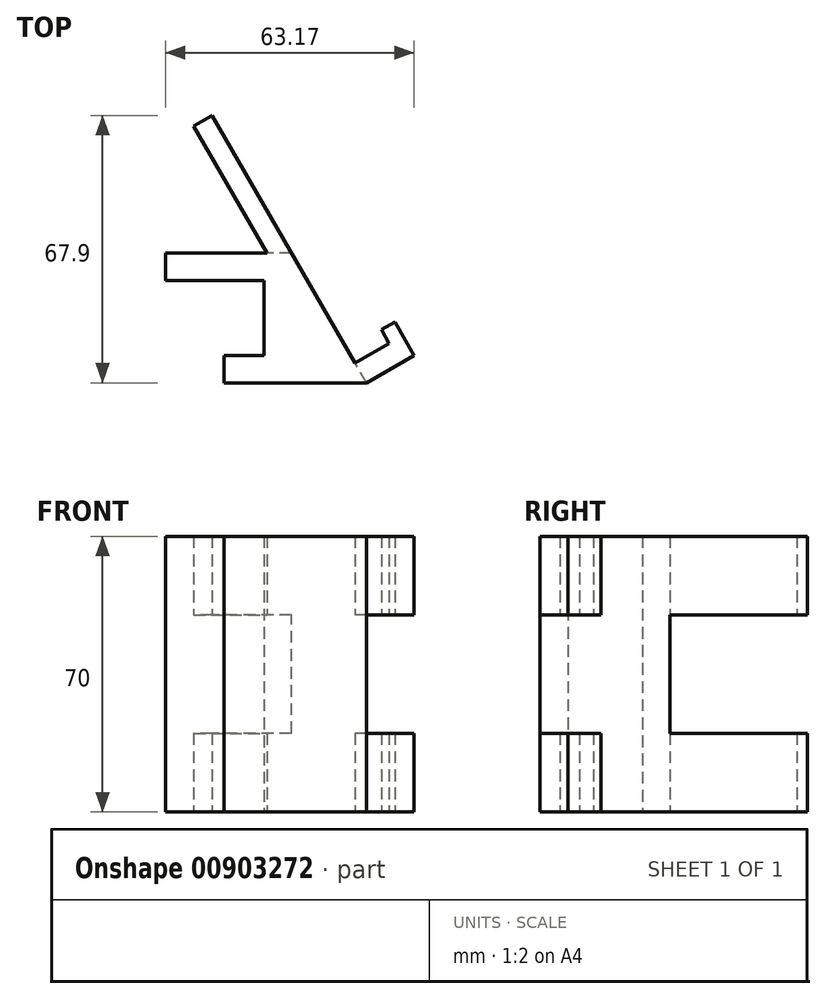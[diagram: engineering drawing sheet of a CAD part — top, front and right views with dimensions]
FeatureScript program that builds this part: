
annotation { "Feature Type Name" : "Feature", "Feature Type Description" : "" }
export const myFeature = defineFeature(function(context is Context, id is Id, definition is map)
    precondition{}
    {
        {
            var Q0;
            Q0=qCreatedBy(makeId("Top.planeOp"),FACE);
            var sketch = newSketch(context, id + "F0", { "sketchPlane" : qUnion([Q0])});
            skLineSegment(sketch, "E0", {"start": v(-43.57, 23.37) * mm, "end": v(-3.06, 23.37) * mm});
            skLineSegment(sketch, "E1", {"start": v(-3.06, 23.37) * mm, "end": v(-3.06, 4.37) * mm});
            skLineSegment(sketch, "E2", {"start": v(-3.06, 4.37) * mm, "end": v(-14.06, 4.37) * mm});
            skLineSegment(sketch, "E3", {"start": v(-14.06, 4.37) * mm, "end": v(-14.06, -10.56) * mm});
            skLineSegment(sketch, "E4", {"start": v(-14.06, -10.56) * mm, "end": v(-29.7, -10.56) * mm});
            skLineSegment(sketch, "E5", {"start": v(-29.7, -10.56) * mm, "end": v(-29.7, 4.37) * mm});
            skLineSegment(sketch, "E6", {"start": v(-29.7, 4.37) * mm, "end": v(-43.57, 4.37) * mm});
            skLineSegment(sketch, "E7", {"start": v(-43.57, 4.37) * mm, "end": v(-43.57, 20.72) * mm});
            skLineSegment(sketch, "E8", {"start": v(-13.06, 4.37) * mm, "end": v(-2.91, 4.37) * mm});
            skLineSegment(sketch, "E9", {"start": v(-2.91, 4.37) * mm, "end": v(-2.91, 23.37) * mm});
            skLineSegment(sketch, "E10", {"start": v(-2.91, 23.37) * mm, "end": v(-27.91, 23.37) * mm});
            skLineSegment(sketch, "E11", {"start": v(-13.06, 4.37) * mm, "end": v(-13.06, -2.63) * mm});
            skLineSegment(sketch, "E12", {"start": v(-13.06, -2.63) * mm, "end": v(4.09, -2.63) * mm});
            skLineSegment(sketch, "E13", {"start": v(4.09, -2.63) * mm, "end": v(4.09, 30.37) * mm});
            skLineSegment(sketch, "E14", {"start": v(4.09, 30.37) * mm, "end": v(-27.91, 30.37) * mm});
            skLineSegment(sketch, "E15", {"start": v(-27.91, 30.37) * mm, "end": v(-27.91, 23.37) * mm});
            skLineSegment(sketch, "E16", {"start": v(23.14, -2.63) * mm, "end": v(4.09, 30.37) * mm});
            skLineSegment(sketch, "E17", {"start": v(4.09, -2.63) * mm, "end": v(23.14, -2.63) * mm});
            skLineSegment(sketch, "E18", {"start": v(23.14, -2.63) * mm, "end": v(31.8, 2.37) * mm});
            skLineSegment(sketch, "E19", {"start": v(31.8, 2.37) * mm, "end": v(28.91, 7.37) * mm});
            skLineSegment(sketch, "E20", {"start": v(28.91, 7.37) * mm, "end": v(20.25, 2.37) * mm});
            skLineSegment(sketch, "E21", {"start": v(4.09, 30.37) * mm, "end": v(-16.06, 65.27) * mm});
            skLineSegment(sketch, "E22", {"start": v(-16.06, 65.27) * mm, "end": v(-20.77, 62.56) * mm});
            skLineSegment(sketch, "E23", {"start": v(-20.77, 62.56) * mm, "end": v(-1.9, 29.86) * mm});
            skLineSegment(sketch, "E24", {"start": v(31.8, 2.37) * mm, "end": v(35.26, 4.37) * mm});
            skLineSegment(sketch, "E25", {"start": v(35.26, 4.37) * mm, "end": v(30.38, 12.83) * mm});
            skLineSegment(sketch, "E26", {"start": v(30.38, 12.83) * mm, "end": v(26.96, 10.86) * mm});
            skLineSegment(sketch, "E27", {"start": v(26.96, 10.86) * mm, "end": v(28.91, 7.37) * mm});
            skSolve(sketch);
        }
        {
            var Q0;
            {var subQ0=sQuery(id+"F0.wireOp",EDGE,"E21");Q0=makeQuery(id+"F0.imprint","IMPRINT",FACE,{"disambiguationData":[TD([[makeQuery(id+"F0.imprint","IMPRINT",EDGE,{"derivedFrom":subQ0}),1.0]])]});}
            var Q1;
            Q1=makeQuery(id+"F0.imprint","IMPRINT",FACE,{"disambiguationData":[TD([[makeQuery(id+"F0.imprint","IMPRINT",EDGE,{"derivedFrom":sQuery(id+"F0.wireOp",EDGE,"E8")}),-1.0]])]});
            var Q2;
            {var subQ0=sQuery(id+"F0.wireOp",EDGE,"E13");Q2=makeQuery(id+"F0.imprint","IMPRINT",FACE,{"disambiguationData":[TD([[makeQuery(id+"F0.imprint","IMPRINT",EDGE,{"derivedFrom":subQ0}),-1.0]])]});}
            var Q3;
            {var subQ0=sQuery(id+"F0.wireOp",EDGE,"E18");Q3=makeQuery(id+"F0.imprint","IMPRINT",FACE,{"disambiguationData":[TD([[makeQuery(id+"F0.imprint","IMPRINT",EDGE,{"derivedFrom":subQ0}),1.0]])]});}
            var Q4;
            Q4=makeQuery(id+"F0.imprint","IMPRINT",FACE,{"disambiguationData":[TD([[makeQuery(id+"F0.imprint","IMPRINT",EDGE,{"derivedFrom":sQuery(id+"F0.wireOp",EDGE,"E19")}),-1.0]])]});
            extrude(context, id + "F1", {"entities" : qUnion([Q0, Q1, Q2, Q3, Q4]), "depth" : 20 * mm, "offsetDistance" : 25 * mm});
        }
        {
            var Q0;
            {var subQ0=sQuery(id+"F0.wireOp",EDGE,"E21");Q0=makeQuery(id+"F0.imprint","IMPRINT",FACE,{"disambiguationData":[TD([[makeQuery(id+"F0.imprint","IMPRINT",EDGE,{"derivedFrom":subQ0}),1.0]])]});}
            var Q1;
            {var subQ10=sQuery(id+"F0.wireOp",EDGE,"E9");Q1=makeQuery(id+"F0.imprint","IMPRINT",FACE,{"disambiguationData":[TD([[makeQuery(id+"F0.imprint","IMPRINT",EDGE,{"derivedFrom":subQ10}),-1.0]])]});}
            var Q2;
            {var subQ0=sQuery(id+"F0.wireOp",EDGE,"E13");Q2=makeQuery(id+"F0.imprint","IMPRINT",FACE,{"disambiguationData":[TD([[makeQuery(id+"F0.imprint","IMPRINT",EDGE,{"derivedFrom":subQ0}),-1.0]])]});}
            var Q3;
            {var subQ0=sQuery(id+"F0.wireOp",EDGE,"E18");Q3=makeQuery(id+"F0.imprint","IMPRINT",FACE,{"disambiguationData":[TD([[makeQuery(id+"F0.imprint","IMPRINT",EDGE,{"derivedFrom":subQ0}),1.0]])]});}
            var Q4;
            Q4=makeQuery(id+"F0.imprint","IMPRINT",FACE,{"disambiguationData":[TD([[makeQuery(id+"F0.imprint","IMPRINT",EDGE,{"derivedFrom":sQuery(id+"F0.wireOp",EDGE,"E19")}),-1.0]])]});
            extrude(context, id + "F2", {"entities" : qUnion([Q0, Q1, Q2, Q3, Q4]), "operationType" : NewBodyOperationType.ADD, "depth" : -50 * mm, "offsetDistance" : 25 * mm});
        }
        {
            var Q0;
            {var subQ0=sQuery(id+"F0.wireOp",EDGE,"E21");Q0=makeQuery(id+"F0.imprint","IMPRINT",FACE,{"disambiguationData":[TD([[makeQuery(id+"F0.imprint","IMPRINT",EDGE,{"derivedFrom":subQ0}),1.0]])]});}
            var Q1;
            {var subQ0=sQuery(id+"F0.wireOp",EDGE,"E18");Q1=makeQuery(id+"F0.imprint","IMPRINT",FACE,{"disambiguationData":[TD([[makeQuery(id+"F0.imprint","IMPRINT",EDGE,{"derivedFrom":subQ0}),1.0]])]});}
            var Q2;
            Q2=makeQuery(id+"F0.imprint","IMPRINT",FACE,{"disambiguationData":[TD([[makeQuery(id+"F0.imprint","IMPRINT",EDGE,{"derivedFrom":sQuery(id+"F0.wireOp",EDGE,"E19")}),-1.0]])]});
            extrude(context, id + "F3", {"entities" : qUnion([Q0, Q1, Q2]), "operationType" : NewBodyOperationType.REMOVE, "oppositeDirection" : true, "depth" : 30 * mm, "offsetDistance" : 25 * mm});
        }
    });
